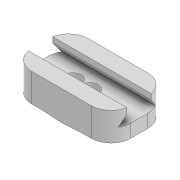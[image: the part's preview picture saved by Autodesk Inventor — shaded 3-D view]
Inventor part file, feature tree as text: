
AUTODESK INVENTOR PART (.ipt)
format: ipt  version: 2022 (Build 260153000, 153)  size: 473,088 bytes
history: native  units: mm
features: sketch x8, extrude x7, fillet x2, projected_geometry x2
ambient origin geometry x8: Origin, YZ Plane, XZ Plane, XY Plane, X Axis, Y Axis, Z Axis, Center Point
bodies: Solid1 (feature_tree)
feature tree (19):
  extrude  "Extrusion1"  Depth=9.0mm
  extrude  "Extrusion2"  Depth=35.0mm
  extrude  "Extrusion3"  Depth=5.0mm TaperAngle=0.0deg
  extrude  "Extrusion4"  Depth=6.0mm
  fillet  "Fillet1"  Radius=6.0mm
  fillet  "Fillet2"  Radius=3.0mm
  extrude  "Extrusion5"  Depth=7.0mm
  extrude  "Extrusion6"  Depth=6.0mm
  sketch  "Sketch7"  dims[d18=5.0mm d19=0.0mm d21=3.0mm]
  extrude  "Extrusion7"  Depth=3.0mm
  sketch  "Sketch1"  dims[d0=12.0mm d1=9.0mm]
  sketch  "Sketch2"  dims[d2=1.0mm d3=0.0mm d4=35.0mm]
  sketch  "Sketch3"  dims[d5=20.0mm d6=5.0mm d7=0.0mm]
  sketch  "Sketch4"  dims[d8=3.0mm d9=0.0mm d10=6.0mm d11=6.0mm d12=3.0mm d13=0.0mm]
  sketch  "Sketch5"  dims[d14=7.0mm d15=5.0mm]
  projected_geometry  "Projected Loop1"
  sketch  "Sketch6"  dims[d16=6.0mm d17=6.0mm]
  projected_geometry  "Projected Loop2"
  sketch  "Sketch8"  dims[d22=3.0mm d23=0.0mm d24=2.0mm d25=2.0mm d26=36.5mm d27=0.0mm d28=0.3mm d29=38.0mm d30=0.0mm d31=8.0mm]
